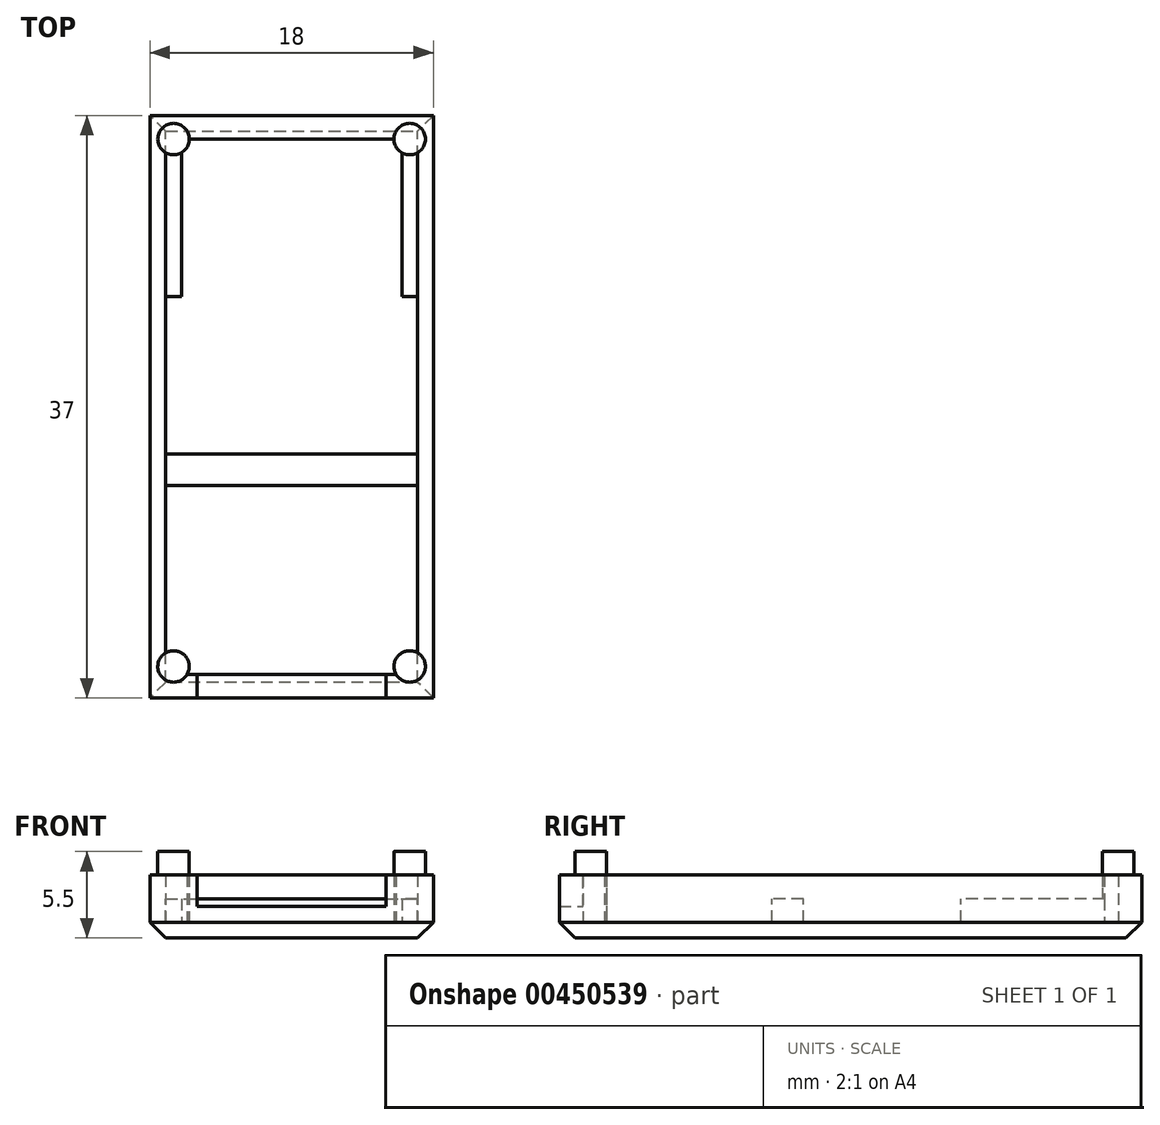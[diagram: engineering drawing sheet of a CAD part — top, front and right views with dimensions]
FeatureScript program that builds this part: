
annotation { "Feature Type Name" : "Feature", "Feature Type Description" : "" }
export const myFeature = defineFeature(function(context is Context, id is Id, definition is map)
    precondition{}
    {
        {
            var Q0;
            Q0=qCreatedBy(makeId("Front.planeOp"),FACE);
            var sketch = newSketch(context, id + "F0", { "sketchPlane" : qUnion([Q0])});
            skLineSegment(sketch, "E0.bottom", {"start": v(-8, 0) * mm, "end": v(8, 0) * mm});
            skLineSegment(sketch, "E0.top", {"start": v(-6, 2) * mm, "end": v(6, 2) * mm});
            skLineSegment(sketch, "E1.top", {"start": v(6, 4) * mm, "end": v(9, 4) * mm});
            skLineSegment(sketch, "E1.left", {"start": v(6, 2) * mm, "end": v(6, 4) * mm});
            skLineSegment(sketch, "E1.right", {"start": v(9, 1) * mm, "end": v(9, 4) * mm});
            skLineSegment(sketch, "E2.top", {"start": v(-6, 4) * mm, "end": v(-9, 4) * mm});
            skLineSegment(sketch, "E2.left", {"start": v(-6, 2) * mm, "end": v(-6, 4) * mm});
            skLineSegment(sketch, "E2.right", {"start": v(-9, 1) * mm, "end": v(-9, 4) * mm});
            skLineSegment(sketch, "E3", {"start": v(-8, 0) * mm, "end": v(-9, 1) * mm});
            skLineSegment(sketch, "E4", {"start": v(8, 0) * mm, "end": v(9, 1) * mm});
            skSolve(sketch);
        }
        {
            var Q0;
            Q0 = qSketchRegion(id + "F0", true);
            extrude(context, id + "F1", {"entities" : qUnion([Q0]), "depth" : 37 * mm});
        }
        {
            var Q0;
            Q0=makeQuery(id+"F1.opExtrude","CAP_FACE",FACE,{"disambiguationData":[OSD([sQuery(id+"F0.wireOp",EDGE,"E0.bottom"),sQuery(id+"F0.wireOp",EDGE,"E0.top"),sQuery(id+"F0.wireOp",EDGE,"E1.top"),sQuery(id+"F0.wireOp",EDGE,"E1.left"),sQuery(id+"F0.wireOp",EDGE,"E1.right"),sQuery(id+"F0.wireOp",EDGE,"E2.top"),sQuery(id+"F0.wireOp",EDGE,"E2.left"),sQuery(id+"F0.wireOp",EDGE,"E2.right"),sQuery(id+"F0.wireOp",EDGE,"E3"),sQuery(id+"F0.wireOp",EDGE,"E4")])],"isStart":true});
            var sketch = newSketch(context, id + "F2", { "sketchPlane" : qUnion([Q0])});
            skLineSegment(sketch, "E5.bottom", {"start": v(-6, 4) * mm, "end": v(6, 4) * mm});
            skLineSegment(sketch, "E5.top", {"start": v(-6, 2) * mm, "end": v(6, 2) * mm});
            skLineSegment(sketch, "E5.left", {"start": v(-6, 4) * mm, "end": v(-6, 2) * mm});
            skLineSegment(sketch, "E5.right", {"start": v(6, 4) * mm, "end": v(6, 2) * mm});
            skSolve(sketch);
        }
        {
            var Q0;
            Q0=makeQuery(id+"F2.imprint","IMPRINT",FACE,{"disambiguationData":[TD([[makeQuery(id+"F2.imprint","IMPRINT",EDGE,{"derivedFrom":sQuery(id+"F2.wireOp",EDGE,"E5.bottom")}),-1.0]])]});
            extrude(context, id + "F3", {"entities" : qUnion([Q0]), "operationType" : NewBodyOperationType.ADD, "oppositeDirection" : true, "depth" : 2 * mm});
        }
        {
            var Q0;
            Q0=makeQuery(id+"F3.boolean.opBoolean","MERGE",FACE,{"derivedFrom":[makeQuery(id+"F1.opExtrude","SWEPT_FACE",FACE,{"disambiguationData":[OSD([sQuery(id+"F0.wireOp",EDGE,"E1.top")])]}),makeQuery(id+"F1.opExtrude","SWEPT_FACE",FACE,{"disambiguationData":[OSD([sQuery(id+"F0.wireOp",EDGE,"E2.top")])]}),makeQuery(id+"F3.opExtrude","SWEPT_FACE",FACE,{"disambiguationData":[OSD([sQuery(id+"F2.wireOp",EDGE,"E5.bottom")])]})]});
            var sketch = newSketch(context, id + "F4", { "sketchPlane" : qUnion([Q0])});
            skLineSegment(sketch, "E6.bottom", {"start": v(-8, -1.5) * mm, "end": v(8, -1.5) * mm});
            skLineSegment(sketch, "E6.top", {"start": v(-8, -35.5) * mm, "end": v(8, -35.5) * mm});
            skLineSegment(sketch, "E6.left", {"start": v(-8, -1.5) * mm, "end": v(-8, -35.5) * mm});
            skLineSegment(sketch, "E6.right", {"start": v(8, -1.5) * mm, "end": v(8, -35.5) * mm});
            skSolve(sketch);
        }
        {
            var Q0;
            Q0 = qSketchRegion(id + "F4", true);
            extrude(context, id + "F5", {"entities" : qUnion([Q0]), "operationType" : NewBodyOperationType.REMOVE, "oppositeDirection" : true, "depth" : 3 * mm});
        }
        {
            var Q0;
            Q0=makeQuery(id+"F1.opExtrude","SWEPT_FACE",FACE,{"disambiguationData":[OSD([sQuery(id+"F0.wireOp",EDGE,"E0.top")])]});
            cPlane(context, id + "F6", {"entities" : qUnion([Q0]), "cplaneType" : CPlaneType.OFFSET, "offset" : .5 * mm, "width" : 152.4 * mm, "height" : 152.4 * mm});
        }
        {
            var Q0;
            Q0=qCreatedBy(id+"F6.planeOp",FACE);
            var sketch = newSketch(context, id + "F7", { "sketchPlane" : qUnion([Q0])});
            skLineSegment(sketch, "E7.bottom", {"start": v(-8, -1.5) * mm, "end": v(-7, -1.5) * mm});
            skLineSegment(sketch, "E7.top", {"start": v(-8, -11.5) * mm, "end": v(-7, -11.5) * mm});
            skLineSegment(sketch, "E7.left", {"start": v(-8, -1.5) * mm, "end": v(-8, -11.5) * mm});
            skLineSegment(sketch, "E7.right", {"start": v(-7, -1.5) * mm, "end": v(-7, -11.5) * mm});
            skLineSegment(sketch, "E8.bottom", {"start": v(8, -1.5) * mm, "end": v(7, -1.5) * mm});
            skLineSegment(sketch, "E8.top", {"start": v(8, -11.5) * mm, "end": v(7, -11.5) * mm});
            skLineSegment(sketch, "E8.left", {"start": v(8, -1.5) * mm, "end": v(8, -11.5) * mm});
            skLineSegment(sketch, "E8.right", {"start": v(7, -1.5) * mm, "end": v(7, -11.5) * mm});
            skLineSegment(sketch, "E9.bottom", {"start": v(-8, -21.5) * mm, "end": v(8, -21.5) * mm});
            skLineSegment(sketch, "E9.top", {"start": v(-8, -23.5) * mm, "end": v(8, -23.5) * mm});
            skLineSegment(sketch, "E9.left", {"start": v(-8, -21.5) * mm, "end": v(-8, -23.5) * mm});
            skLineSegment(sketch, "E9.right", {"start": v(8, -21.5) * mm, "end": v(8, -23.5) * mm});
            skSolve(sketch);
        }
        {
            var Q0;
            Q0 = qSketchRegion(id + "F7", true);
            var Q1;
            Q1=makeQuery(id+"F5.boolean.opBoolean","COPY",FACE,{"derivedFrom":makeQuery(id+"F5.opExtrude","CAP_FACE",FACE,{"disambiguationData":[OSD([sQuery(id+"F4.wireOp",EDGE,"E6.bottom"),sQuery(id+"F4.wireOp",EDGE,"E6.top"),sQuery(id+"F4.wireOp",EDGE,"E6.left"),sQuery(id+"F4.wireOp",EDGE,"E6.right")])],"isStart":false})});
            extrude(context, id + "F8", {"entities" : qUnion([Q0]), "operationType" : NewBodyOperationType.ADD, "endBound" : BoundingType.UP_TO_SURFACE, "oppositeDirection" : true, "endBoundEntityFace" : qUnion([Q1]), "depth" : 25.4 * mm});
        }
        {
            var Q0;
            Q0=makeQuery(id+"F1.opExtrude","CAP_EDGE",EDGE,{"disambiguationData":[OSD([sQuery(id+"F0.wireOp",EDGE,"E0.bottom")])],"isStart":true});
            var Q1;
            Q1=makeQuery(id+"F1.opExtrude","CAP_EDGE",EDGE,{"disambiguationData":[OSD([sQuery(id+"F0.wireOp",EDGE,"E0.bottom")])],"isStart":false});
            chamfer(context, id + "F9", {"entities" : qUnion([Q0, Q1]), "width" : 1 * mm, "tangentPropagation" : true});
        }
        {
            var Q0;
            Q0=makeQuery(id+"F3.boolean.opBoolean","MERGE",FACE,{"derivedFrom":[makeQuery(id+"F1.opExtrude","SWEPT_FACE",FACE,{"disambiguationData":[OSD([sQuery(id+"F0.wireOp",EDGE,"E1.top")])]}),makeQuery(id+"F1.opExtrude","SWEPT_FACE",FACE,{"disambiguationData":[OSD([sQuery(id+"F0.wireOp",EDGE,"E2.top")])]}),makeQuery(id+"F3.opExtrude","SWEPT_FACE",FACE,{"disambiguationData":[OSD([sQuery(id+"F2.wireOp",EDGE,"E5.bottom")])]})]});
            var sketch = newSketch(context, id + "F10", { "sketchPlane" : qUnion([Q0])});
            skCircle(sketch, "E10", {"center": v(7.5, -35) * mm, "radius": 1 * mm});
            skCircle(sketch, "E11", {"center": v(-7.5, -35) * mm, "radius": 1 * mm});
            skCircle(sketch, "E12", {"center": v(-7.5, -1.5) * mm, "radius": 1 * mm});
            skCircle(sketch, "E13", {"center": v(7.5, -1.5) * mm, "radius": 1 * mm});
            skSolve(sketch);
        }
        {
            var Q0;
            Q0 = qSketchRegion(id + "F10", true);
            var Q1;
            {var subQ0=sQuery(id+"F4.wireOp",EDGE,"E6.right");var subQ1=sQuery(id+"F4.wireOp",EDGE,"E6.left");var subQ2=sQuery(id+"F4.wireOp",EDGE,"E6.bottom");Q1=makeQuery(id+"F8.boolean.opBoolean","SPLIT",FACE,{"disambiguationData":[TD([makeQuery(id+"F5.boolean.opBoolean","COPY",FACE,{"derivedFrom":makeQuery(id+"F5.opExtrude","SWEPT_FACE",FACE,{"disambiguationData":[OSD([subQ2])]})})])],"derivedFrom":makeQuery(id+"F5.boolean.opBoolean","COPY",FACE,{"derivedFrom":makeQuery(id+"F5.opExtrude","CAP_FACE",FACE,{"disambiguationData":[OSD([subQ2,sQuery(id+"F4.wireOp",EDGE,"E6.top"),subQ1,subQ0])],"isStart":false})})});}
            extrude(context, id + "F11", {"entities" : qUnion([Q0]), "operationType" : NewBodyOperationType.ADD, "depth" : 1.5 * mm, "hasSecondDirection" : true, "secondDirectionBound" : SecondDirectionBoundingType.UP_TO_SURFACE, "secondDirectionOppositeDirection" : true, "secondDirectionBoundEntityFace" : qUnion([Q1]), "secondDirectionDepth" : 25.4 * mm});
        }
    });
